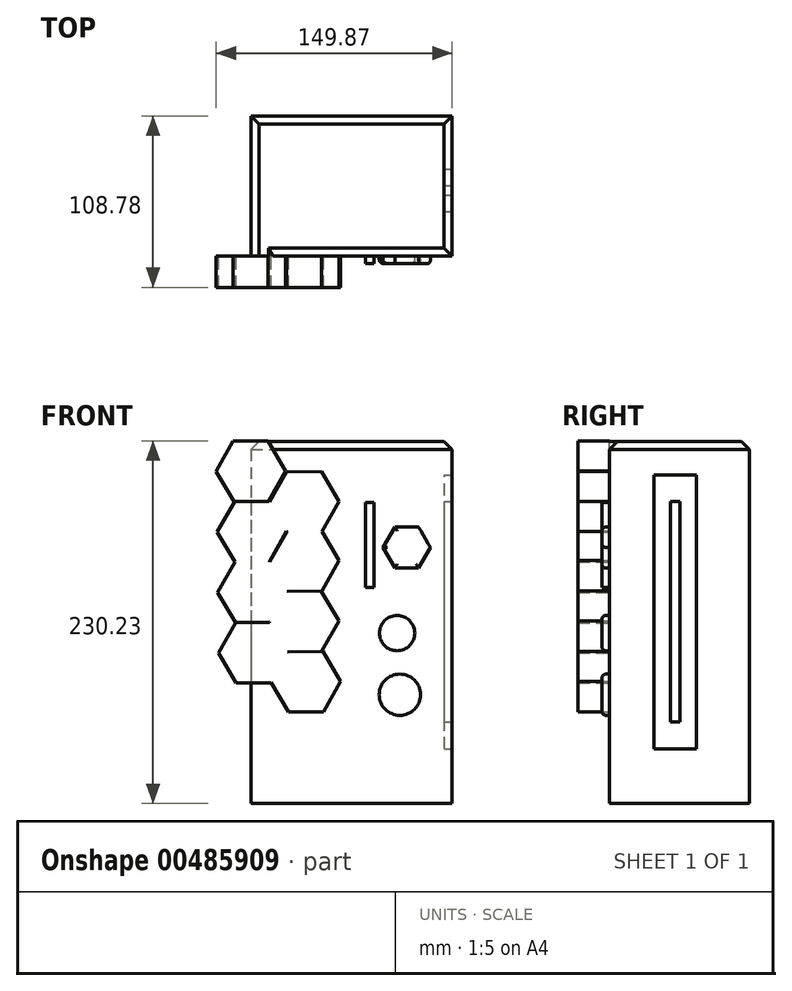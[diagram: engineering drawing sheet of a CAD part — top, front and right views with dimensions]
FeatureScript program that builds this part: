
annotation { "Feature Type Name" : "Feature", "Feature Type Description" : "" }
export const myFeature = defineFeature(function(context is Context, id is Id, definition is map)
    precondition{}
    {
        {
            var Q0;
            Q0=qCreatedBy(makeId("Top.planeOp"),FACE);
            var sketch = newSketch(context, id + "F0", { "sketchPlane" : qUnion([Q0])});
            skLineSegment(sketch, "E0.bottom", {"start": v(63.88, -44.4) * mm, "end": v(-63.88, -44.4) * mm});
            skLineSegment(sketch, "E0.top", {"start": v(63.88, 44.4) * mm, "end": v(-63.88, 44.4) * mm});
            skLineSegment(sketch, "E0.left", {"start": v(63.88, -44.4) * mm, "end": v(63.88, 44.4) * mm});
            skLineSegment(sketch, "E0.right", {"start": v(-63.88, -44.4) * mm, "end": v(-63.88, 44.4) * mm});
            skPoint(sketch, "E0.middle", {"position": v(0, 0) * mm});
            skSolve(sketch);
        }
        {
            var Q0;
            Q0=makeQuery(id+"F0.imprint","IMPRINT",FACE,{"disambiguationData":[TD([[makeQuery(id+"F0.imprint","IMPRINT",EDGE,{"derivedFrom":sQuery(id+"F0.wireOp",EDGE,"E0.bottom")}),-1.0]])]});
            extrude(context, id + "F1", {"entities" : qUnion([Q0]), "depth" : 230 * mm});
        }
        {
            var Q0;
            Q0=makeQuery(id+"F1.opExtrude","SWEPT_FACE",FACE,{"disambiguationData":[OSD([sQuery(id+"F0.wireOp",EDGE,"E0.bottom")])]});
            var sketch = newSketch(context, id + "F2", { "sketchPlane" : qUnion([Q0])});
            skCircle(sketch, "E1.cCircle", {"center": v(-63.88, 210.98) * mm, "radius": 19.15 * mm, "construction": true});
            skLineSegment(sketch, "E1.0", {"start": v(-41.77, 211.18) * mm, "end": v(-52.65, 191.93) * mm});
            skLineSegment(sketch, "E1.1", {"start": v(-52.65, 191.93) * mm, "end": v(-74.76, 191.73) * mm});
            skLineSegment(sketch, "E1.2", {"start": v(-74.76, 191.73) * mm, "end": v(-85.99, 210.77) * mm});
            skLineSegment(sketch, "E1.3", {"start": v(-85.99, 210.77) * mm, "end": v(-75.1, 230.02) * mm});
            skLineSegment(sketch, "E1.4", {"start": v(-75.1, 230.02) * mm, "end": v(-53, 230.23) * mm});
            skLineSegment(sketch, "E1.5", {"start": v(-53, 230.23) * mm, "end": v(-41.77, 211.18) * mm});
            skPoint(sketch, "E1.0.midPoint", {"position": v(-47.2, 201.56) * mm});
            skSolve(sketch);
        }
        {
            var Q0;
            {var subQ3=sQuery(id+"F2.wireOp",EDGE,"E1.0");Q0=makeQuery(id+"F2.imprint","IMPRINT",FACE,{"disambiguationData":[TD([[makeQuery(id+"F2.imprint","IMPRINT",EDGE,{"derivedFrom":subQ3}),1.0]])]});}
            var sketch = newSketch(context, id + "F3", { "sketchPlane" : qUnion([Q0])});
            skCircle(sketch, "E2.cCircle", {"center": v(-63.2, 172.48) * mm, "radius": 19.15 * mm, "construction": true});
            skLineSegment(sketch, "E2.0", {"start": v(-41.09, 172.69) * mm, "end": v(-51.96, 153.44) * mm});
            skLineSegment(sketch, "E2.1", {"start": v(-51.96, 153.44) * mm, "end": v(-74.07, 153.23) * mm});
            skLineSegment(sketch, "E2.2", {"start": v(-74.07, 153.23) * mm, "end": v(-85.3, 172.28) * mm});
            skLineSegment(sketch, "E2.3", {"start": v(-85.3, 172.28) * mm, "end": v(-74.43, 191.53) * mm});
            skLineSegment(sketch, "E2.4", {"start": v(-74.43, 191.53) * mm, "end": v(-52.32, 191.73) * mm});
            skLineSegment(sketch, "E2.5", {"start": v(-52.32, 191.73) * mm, "end": v(-41.09, 172.69) * mm});
            skPoint(sketch, "E2.0.midPoint", {"position": v(-46.52, 163.06) * mm});
            skCircle(sketch, "E3.cCircle", {"center": v(-62.84, 134.19) * mm, "radius": 19.15 * mm, "construction": true});
            skLineSegment(sketch, "E3.0", {"start": v(-40.73, 134.4) * mm, "end": v(-51.61, 115.14) * mm});
            skLineSegment(sketch, "E3.1", {"start": v(-51.61, 115.14) * mm, "end": v(-73.72, 114.94) * mm});
            skLineSegment(sketch, "E3.2", {"start": v(-73.72, 114.94) * mm, "end": v(-84.95, 133.98) * mm});
            skLineSegment(sketch, "E3.3", {"start": v(-84.95, 133.98) * mm, "end": v(-74.07, 153.23) * mm});
            skLineSegment(sketch, "E3.4", {"start": v(-74.07, 153.23) * mm, "end": v(-51.96, 153.44) * mm});
            skLineSegment(sketch, "E3.5", {"start": v(-51.96, 153.44) * mm, "end": v(-40.73, 134.4) * mm});
            skPoint(sketch, "E3.0.midPoint", {"position": v(-46.17, 124.77) * mm});
            skCircle(sketch, "E4.cCircle", {"center": v(-62.33, 95.65) * mm, "radius": 19.15 * mm, "construction": true});
            skLineSegment(sketch, "E4.0", {"start": v(-40.22, 95.86) * mm, "end": v(-51.1, 76.6) * mm});
            skLineSegment(sketch, "E4.1", {"start": v(-51.1, 76.6) * mm, "end": v(-73.2, 76.4) * mm});
            skLineSegment(sketch, "E4.2", {"start": v(-73.2, 76.4) * mm, "end": v(-84.44, 95.45) * mm});
            skLineSegment(sketch, "E4.3", {"start": v(-84.44, 95.45) * mm, "end": v(-73.56, 114.7) * mm});
            skLineSegment(sketch, "E4.4", {"start": v(-73.56, 114.7) * mm, "end": v(-51.45, 114.9) * mm});
            skLineSegment(sketch, "E4.5", {"start": v(-51.45, 114.9) * mm, "end": v(-40.22, 95.86) * mm});
            skPoint(sketch, "E4.0.midPoint", {"position": v(-45.65, 86.23) * mm});
            skCircle(sketch, "E5.cCircle", {"center": v(-30.08, 191.57) * mm, "radius": 19.15 * mm, "construction": true});
            skLineSegment(sketch, "E5.0", {"start": v(-7.97, 191.77) * mm, "end": v(-18.85, 172.52) * mm});
            skLineSegment(sketch, "E5.1", {"start": v(-18.85, 172.52) * mm, "end": v(-40.96, 172.32) * mm});
            skLineSegment(sketch, "E5.2", {"start": v(-40.96, 172.32) * mm, "end": v(-52.19, 191.36) * mm});
            skLineSegment(sketch, "E5.3", {"start": v(-52.19, 191.36) * mm, "end": v(-41.31, 210.61) * mm});
            skLineSegment(sketch, "E5.4", {"start": v(-41.31, 210.61) * mm, "end": v(-19.2, 210.82) * mm});
            skLineSegment(sketch, "E5.5", {"start": v(-19.2, 210.82) * mm, "end": v(-7.97, 191.77) * mm});
            skPoint(sketch, "E5.0.midPoint", {"position": v(-13.4, 182.15) * mm});
            skCircle(sketch, "E6.cCircle", {"center": v(-30.12, 154) * mm, "radius": 19.15 * mm, "construction": true});
            skLineSegment(sketch, "E6.0", {"start": v(-8, 154.2) * mm, "end": v(-18.88, 134.95) * mm});
            skLineSegment(sketch, "E6.1", {"start": v(-18.88, 134.95) * mm, "end": v(-41, 134.74) * mm});
            skLineSegment(sketch, "E6.2", {"start": v(-41, 134.74) * mm, "end": v(-52.23, 153.79) * mm});
            skLineSegment(sketch, "E6.3", {"start": v(-52.23, 153.79) * mm, "end": v(-41.35, 173.04) * mm});
            skLineSegment(sketch, "E6.4", {"start": v(-41.35, 173.04) * mm, "end": v(-19.24, 173.24) * mm});
            skLineSegment(sketch, "E6.5", {"start": v(-19.24, 173.24) * mm, "end": v(-8, 154.2) * mm});
            skPoint(sketch, "E6.0.midPoint", {"position": v(-13.44, 144.57) * mm});
            skCircle(sketch, "E7.cCircle", {"center": v(-30.13, 115.57) * mm, "radius": 19.15 * mm, "construction": true});
            skLineSegment(sketch, "E7.0", {"start": v(-8.02, 115.77) * mm, "end": v(-18.9, 96.52) * mm});
            skLineSegment(sketch, "E7.1", {"start": v(-18.9, 96.52) * mm, "end": v(-41, 96.32) * mm});
            skLineSegment(sketch, "E7.2", {"start": v(-41, 96.32) * mm, "end": v(-52.24, 115.36) * mm});
            skLineSegment(sketch, "E7.3", {"start": v(-52.24, 115.36) * mm, "end": v(-41.36, 134.61) * mm});
            skLineSegment(sketch, "E7.4", {"start": v(-41.36, 134.61) * mm, "end": v(-19.25, 134.82) * mm});
            skLineSegment(sketch, "E7.5", {"start": v(-19.25, 134.82) * mm, "end": v(-8.02, 115.77) * mm});
            skPoint(sketch, "E7.0.midPoint", {"position": v(-13.46, 106.15) * mm});
            skCircle(sketch, "E8.cCircle", {"center": v(-29.1, 77.25) * mm, "radius": 19.15 * mm, "construction": true});
            skLineSegment(sketch, "E8.0", {"start": v(-6.99, 77.46) * mm, "end": v(-17.86, 58.2) * mm});
            skLineSegment(sketch, "E8.1", {"start": v(-17.86, 58.2) * mm, "end": v(-39.97, 58) * mm});
            skLineSegment(sketch, "E8.2", {"start": v(-39.97, 58) * mm, "end": v(-51.2, 77.05) * mm});
            skLineSegment(sketch, "E8.3", {"start": v(-51.2, 77.05) * mm, "end": v(-40.33, 96.3) * mm});
            skLineSegment(sketch, "E8.4", {"start": v(-40.33, 96.3) * mm, "end": v(-18.22, 96.5) * mm});
            skLineSegment(sketch, "E8.5", {"start": v(-18.22, 96.5) * mm, "end": v(-6.99, 77.46) * mm});
            skPoint(sketch, "E8.0.midPoint", {"position": v(-12.43, 67.83) * mm});
            skSolve(sketch);
        }
        {
            var Q0;
            Q0 = qSketchRegion(id + "F3", true);
            extrude(context, id + "F4", {"entities" : qUnion([Q0]), "operationType" : NewBodyOperationType.ADD, "depth" : 20 * mm});
        }
        {
            var Q0;
            Q0 = qSketchRegion(id + "F2", true);
            extrude(context, id + "F5", {"entities" : qUnion([Q0]), "operationType" : NewBodyOperationType.ADD, "depth" : 19.99 * mm});
        }
        {
            var Q0;
            Q0=makeQuery(id+"F1.opExtrude","SWEPT_FACE",FACE,{"disambiguationData":[OSD([sQuery(id+"F0.wireOp",EDGE,"E0.left")])]});
            var sketch = newSketch(context, id + "F6", { "sketchPlane" : qUnion([Q0])});
            skLineSegment(sketch, "E9.bottom", {"start": v(10.87, 34.68) * mm, "end": v(-16.09, 34.68) * mm});
            skLineSegment(sketch, "E9.top", {"start": v(10.87, 208.6) * mm, "end": v(-16.09, 208.6) * mm});
            skLineSegment(sketch, "E9.left", {"start": v(10.87, 34.68) * mm, "end": v(10.87, 208.6) * mm});
            skLineSegment(sketch, "E9.right", {"start": v(-16.09, 34.68) * mm, "end": v(-16.09, 208.6) * mm});
            skPoint(sketch, "E9.middle", {"position": v(-2.6, 121.64) * mm});
            skLineSegment(sketch, "E10.bottom", {"start": v(0.43, 51.64) * mm, "end": v(-5.65, 51.64) * mm});
            skLineSegment(sketch, "E10.top", {"start": v(0.43, 191.64) * mm, "end": v(-5.65, 191.64) * mm});
            skLineSegment(sketch, "E10.left", {"start": v(0.43, 51.64) * mm, "end": v(0.43, 191.64) * mm});
            skLineSegment(sketch, "E10.right", {"start": v(-5.65, 51.64) * mm, "end": v(-5.65, 191.64) * mm});
            skSolve(sketch);
        }
        {
            var Q0;
            Q0 = qSketchRegion(id + "F6", true);
            extrude(context, id + "F7", {"entities" : qUnion([Q0]), "operationType" : NewBodyOperationType.REMOVE, "oppositeDirection" : true, "depth" : 4.83 * mm});
        }
        {
            var Q0;
            {var subQ0=sQuery(id+"F0.wireOp",EDGE,"E0.bottom");Q0=makeQuery(id+"F5.boolean.opBoolean","SPLIT",EDGE,{"disambiguationData":[topologyDisambiguationEdgeConnected([makeQuery(id+"F1.opExtrude","SWEPT_FACE",FACE,{"disambiguationData":[OSD([subQ0])]})])],"derivedFrom":makeQuery(id+"F1.opExtrude","CAP_EDGE",EDGE,{"disambiguationData":[OSD([subQ0])],"isStart":false})});}
            var Q1;
            Q1=makeQuery(id+"F1.opExtrude","CAP_EDGE",EDGE,{"disambiguationData":[OSD([sQuery(id+"F0.wireOp",EDGE,"E0.left")])],"isStart":false});
            var Q2;
            Q2=makeQuery(id+"F1.opExtrude","CAP_EDGE",EDGE,{"disambiguationData":[OSD([sQuery(id+"F0.wireOp",EDGE,"E0.top")])],"isStart":false});
            var Q3;
            Q3=makeQuery(id+"F1.opExtrude","CAP_EDGE",EDGE,{"disambiguationData":[OSD([sQuery(id+"F0.wireOp",EDGE,"E0.right")])],"isStart":false});
            chamfer(context, id + "F8", {"entities" : qUnion([Q0, Q1, Q2, Q3]), "width" : 5.08 * mm, "tangentPropagation" : true});
        }
        {
            var Q0;
            {var subQ8=sQuery(id+"F0.wireOp",EDGE,"E0.left");var subQ12=sQuery(id+"F0.wireOp",EDGE,"E0.bottom");Q0=makeQuery(id+"F4.boolean.opBoolean","SPLIT",FACE,{"disambiguationData":[TD([makeQuery(id+"F1.opExtrude","SWEPT_FACE",FACE,{"disambiguationData":[OSD([subQ8])]})])],"derivedFrom":makeQuery(id+"F1.opExtrude","SWEPT_FACE",FACE,{"disambiguationData":[OSD([subQ12])]})});}
            var sketch = newSketch(context, id + "F9", { "sketchPlane" : qUnion([Q0])});
            skCircle(sketch, "E11", {"center": v(30.68, 69.03) * mm, "radius": 13.08 * mm});
            skCircle(sketch, "E12", {"center": v(28.94, 108.16) * mm, "radius": 11.22 * mm});
            skLineSegment(sketch, "E13.bottom", {"start": v(14.16, 137.29) * mm, "end": v(8.94, 137.29) * mm});
            skLineSegment(sketch, "E13.top", {"start": v(14.16, 191.2) * mm, "end": v(8.94, 191.2) * mm});
            skLineSegment(sketch, "E13.left", {"start": v(14.16, 137.29) * mm, "end": v(14.16, 191.2) * mm});
            skLineSegment(sketch, "E13.right", {"start": v(8.94, 137.29) * mm, "end": v(8.94, 191.2) * mm});
            skPoint(sketch, "E13.middle", {"position": v(11.55, 164.24) * mm});
            skCircle(sketch, "E14.cCircle", {"center": v(35.03, 162.5) * mm, "radius": 13.04 * mm, "construction": true});
            skLineSegment(sketch, "E14.0", {"start": v(42.56, 149.46) * mm, "end": v(27.5, 149.46) * mm});
            skLineSegment(sketch, "E14.1", {"start": v(27.5, 149.46) * mm, "end": v(19.97, 162.5) * mm});
            skLineSegment(sketch, "E14.2", {"start": v(19.97, 162.5) * mm, "end": v(27.5, 175.55) * mm});
            skLineSegment(sketch, "E14.3", {"start": v(27.5, 175.55) * mm, "end": v(42.56, 175.55) * mm});
            skLineSegment(sketch, "E14.4", {"start": v(42.56, 175.55) * mm, "end": v(50.1, 162.5) * mm});
            skLineSegment(sketch, "E14.5", {"start": v(50.1, 162.5) * mm, "end": v(42.56, 149.46) * mm});
            skPoint(sketch, "E14.0.midPoint", {"position": v(35.03, 149.46) * mm});
            skSolve(sketch);
        }
        {
            var Q0;
            Q0 = qSketchRegion(id + "F9", true);
            extrude(context, id + "F10", {"entities" : qUnion([Q0]), "operationType" : NewBodyOperationType.ADD, "depth" : 4.83 * mm});
        }
        {
            var Q0;
            Q0=makeQuery(id+"F10.opExtrude","CAP_EDGE",EDGE,{"disambiguationData":[OSD([sQuery(id+"F9.wireOp",EDGE,"E14.3")])],"isStart":false});
            var Q1;
            Q1=makeQuery(id+"F10.opExtrude","CAP_EDGE",EDGE,{"disambiguationData":[OSD([sQuery(id+"F9.wireOp",EDGE,"E14.5")])],"isStart":false});
            var Q2;
            Q2=makeQuery(id+"F10.opExtrude","CAP_EDGE",EDGE,{"disambiguationData":[OSD([sQuery(id+"F9.wireOp",EDGE,"E14.0")])],"isStart":false});
            var Q3;
            Q3=makeQuery(id+"F10.opExtrude","CAP_EDGE",EDGE,{"disambiguationData":[OSD([sQuery(id+"F9.wireOp",EDGE,"E14.1")])],"isStart":false});
            var Q4;
            Q4=makeQuery(id+"F10.opExtrude","CAP_EDGE",EDGE,{"disambiguationData":[OSD([sQuery(id+"F9.wireOp",EDGE,"E14.2")])],"isStart":false});
            var Q5;
            Q5=makeQuery(id+"F10.opExtrude","CAP_EDGE",EDGE,{"disambiguationData":[OSD([sQuery(id+"F9.wireOp",EDGE,"E12")])],"isStart":false});
            var Q6;
            Q6=makeQuery(id+"F10.opExtrude","CAP_EDGE",EDGE,{"disambiguationData":[OSD([sQuery(id+"F9.wireOp",EDGE,"E11")])],"isStart":false});
            fillet(context, id + "F11", {"entities" : qUnion([Q0, Q1, Q2, Q3, Q4, Q5, Q6]), "radius" : 2.54 * mm, "tangentPropagation" : true, "allowEdgeOverflow" : false});
        }
    });
